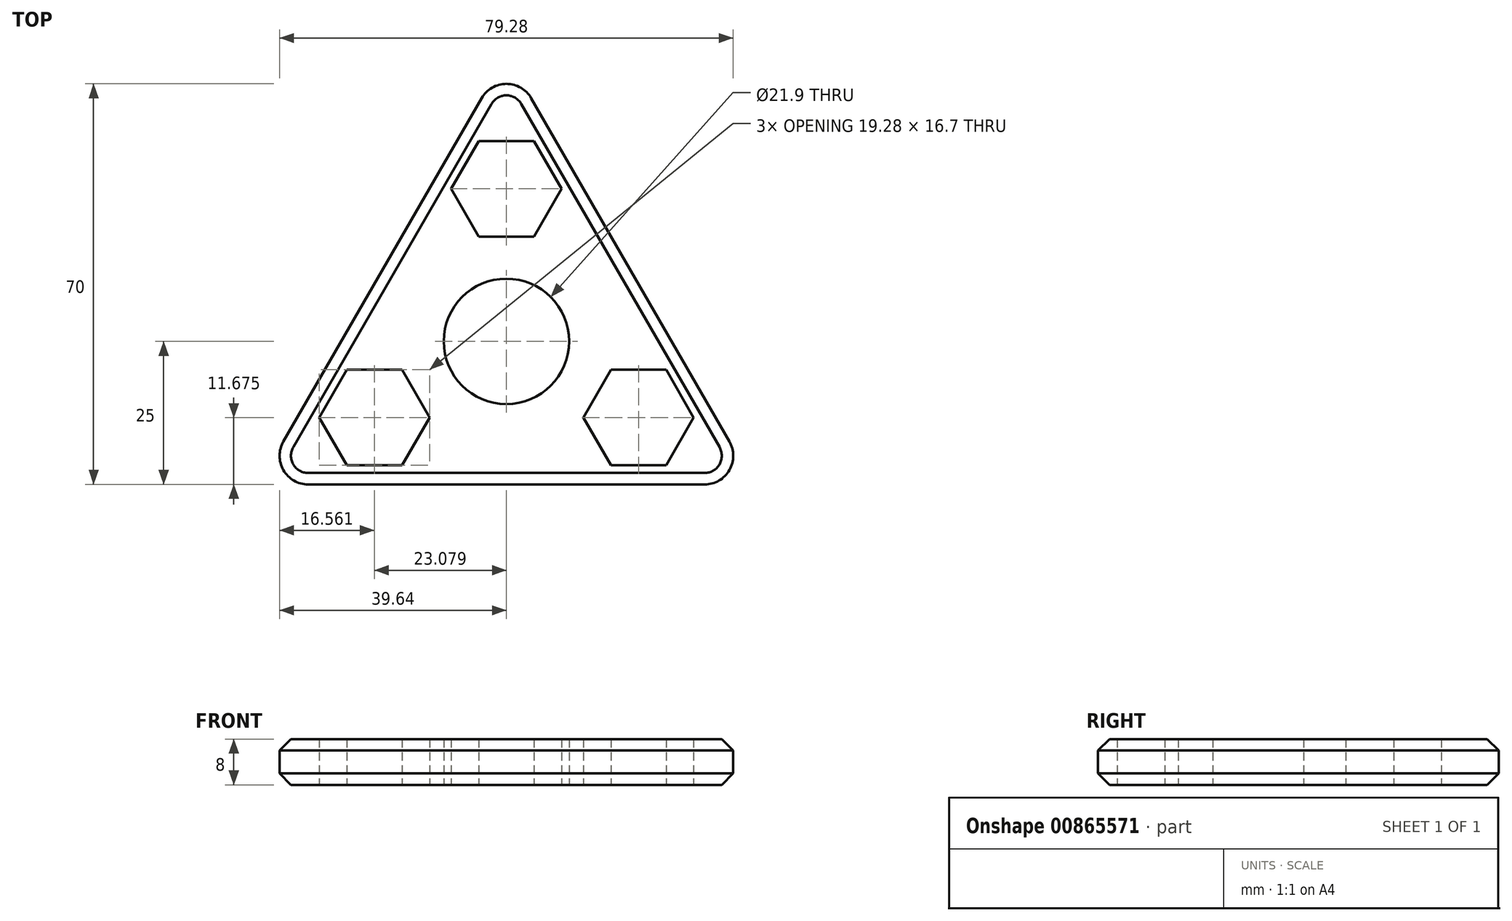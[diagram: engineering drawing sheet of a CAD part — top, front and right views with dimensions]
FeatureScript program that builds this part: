
annotation { "Feature Type Name" : "Feature", "Feature Type Description" : "" }
export const myFeature = defineFeature(function(context is Context, id is Id, definition is map)
    precondition{}
    {
        {
            var Q0;
            Q0=qCreatedBy(makeId("Top.planeOp"),FACE);
            var sketch = newSketch(context, id + "F0", { "sketchPlane" : qUnion([Q0])});
            skCircle(sketch, "E0", {"center": v(0, 0) * mm, "radius": 10.95 * mm});
            skCircle(sketch, "E1.cCircle", {"center": v(0, 26.65) * mm, "radius": 8.35 * mm, "construction": true});
            skLineSegment(sketch, "E1.0", {"start": v(4.82, 18.3) * mm, "end": v(-4.82, 18.3) * mm});
            skLineSegment(sketch, "E1.1", {"start": v(-4.82, 18.3) * mm, "end": v(-9.64, 26.65) * mm});
            skLineSegment(sketch, "E1.2", {"start": v(-9.64, 26.65) * mm, "end": v(-4.82, 35) * mm});
            skLineSegment(sketch, "E1.3", {"start": v(-4.82, 35) * mm, "end": v(4.82, 35) * mm});
            skLineSegment(sketch, "E1.4", {"start": v(4.82, 35) * mm, "end": v(9.64, 26.65) * mm});
            skLineSegment(sketch, "E1.5", {"start": v(9.64, 26.65) * mm, "end": v(4.82, 18.3) * mm});
            skPoint(sketch, "E1.0.midPoint", {"position": v(0, 18.3) * mm});
            skCircle(sketch, "E2", {"center": v(0, 0) * mm, "radius": 26.65 * mm, "construction": true});
            skLineSegment(sketch, "E3.2.1", {"start": v(-27.9, -21.67) * mm, "end": v(-32.72, -13.32) * mm});
            skLineSegment(sketch, "E3.2.2", {"start": v(-18.26, -21.67) * mm, "end": v(-27.9, -21.67) * mm});
            skLineSegment(sketch, "E3.2.3", {"start": v(-13.44, -13.32) * mm, "end": v(-18.26, -21.67) * mm});
            skLineSegment(sketch, "E3.2.4", {"start": v(-18.26, -4.97) * mm, "end": v(-13.44, -13.32) * mm});
            skLineSegment(sketch, "E3.2.5", {"start": v(-27.9, -4.97) * mm, "end": v(-18.26, -4.97) * mm});
            skLineSegment(sketch, "E3.2.6", {"start": v(-32.72, -13.32) * mm, "end": v(-27.9, -4.97) * mm});
            skLineSegment(sketch, "E4.2.4.0", {"start": v(32.72, -13.33) * mm, "end": v(27.9, -21.68) * mm});
            skLineSegment(sketch, "E4.5.4.0", {"start": v(27.9, -4.98) * mm, "end": v(32.72, -13.33) * mm});
            skLineSegment(sketch, "E4.8.4.0", {"start": v(18.26, -4.98) * mm, "end": v(27.9, -4.98) * mm});
            skLineSegment(sketch, "E4.11.4.0", {"start": v(13.44, -13.33) * mm, "end": v(18.26, -4.98) * mm});
            skLineSegment(sketch, "E4.14.4.0", {"start": v(18.26, -21.68) * mm, "end": v(13.44, -13.33) * mm});
            skLineSegment(sketch, "E4.17.4.0", {"start": v(27.9, -21.68) * mm, "end": v(18.26, -21.68) * mm});
            skLineSegment(sketch, "E5", {"start": v(-27.4, 15.83) * mm, "end": v(0, 0) * mm, "construction": true});
            skLineSegment(sketch, "E6", {"start": v(27.4, 15.82) * mm, "end": v(0, 0) * mm, "construction": true});
            skLineSegment(sketch, "E7", {"start": v(0, 0) * mm, "end": v(0, -31.65) * mm, "construction": true});
            skPoint(sketch, "E8.first.point", {"position": v(-10.32, 24.57) * mm});
            skPoint(sketch, "E8.second.point", {"position": v(-16.58, 9.57) * mm});
            skPoint(sketch, "E8.third.point", {"position": v(-26.44, -3.35) * mm});
            skCircle(sketch, "E9.cCircle", {"center": v(0, 0) * mm, "radius": 25 * mm, "construction": true});
            skLineSegment(sketch, "E9.0", {"start": v(4.33, 42.5) * mm, "end": v(38.97, -17.5) * mm});
            skLineSegment(sketch, "E9.1", {"start": v(34.64, -25) * mm, "end": v(-34.64, -25) * mm});
            skLineSegment(sketch, "E9.2", {"start": v(-38.97, -17.5) * mm, "end": v(-4.33, 42.5) * mm});
            skPoint(sketch, "E9.0.midPoint", {"position": v(0, 47.42) * mm});
            skPoint(sketch, "E10.visualSharp", {"position": v(-43.3, -25) * mm});
            skArc(sketch, "E10.filletArc", {"start": v(-38.97, -17.5) * mm, "mid": v(-38.97, -22.5) * mm, "end": v(-34.64, -25) * mm});
            skPoint(sketch, "E11.visualSharp", {"position": v(43.3, -25) * mm});
            skArc(sketch, "E11.filletArc", {"start": v(34.64, -25) * mm, "mid": v(38.97, -22.5) * mm, "end": v(38.97, -17.5) * mm});
            skPoint(sketch, "E12.visualSharp", {"position": v(0, 50) * mm});
            skArc(sketch, "E12.filletArc", {"start": v(4.33, 42.5) * mm, "mid": v(0, 45) * mm, "end": v(-4.33, 42.5) * mm});
            skSolve(sketch);
        }
        {
            var Q0;
            Q0=qSketchRegion(id+"F0",true);
            extrude(context, id + "F1", {"entities" : qUnion([Q0]), "endBound" : BoundingType.SYMMETRIC, "depth" : 8 * mm, "offsetDistance" : 25 * mm});
        }
        {
            var Q0;
            Q0=makeQuery(id+"F1.opExtrude","CAP_EDGE",EDGE,{"disambiguationData":[OSD([sQuery(id+"F0.wireOp",EDGE,"E9.2")])],"isStart":false});
            var Q1;
            Q1=makeQuery(id+"F1.opExtrude","CAP_EDGE",EDGE,{"disambiguationData":[OSD([sQuery(id+"F0.wireOp",EDGE,"E9.0")])],"isStart":false});
            var Q2;
            Q2=makeQuery(id+"F1.opExtrude","CAP_EDGE",EDGE,{"disambiguationData":[OSD([sQuery(id+"F0.wireOp",EDGE,"E9.2")])],"isStart":true});
            chamfer(context, id + "F2", {"entities" : qUnion([Q0, Q1, Q2]), "width" : 2 * mm, "tangentPropagation" : true});
        }
    });
